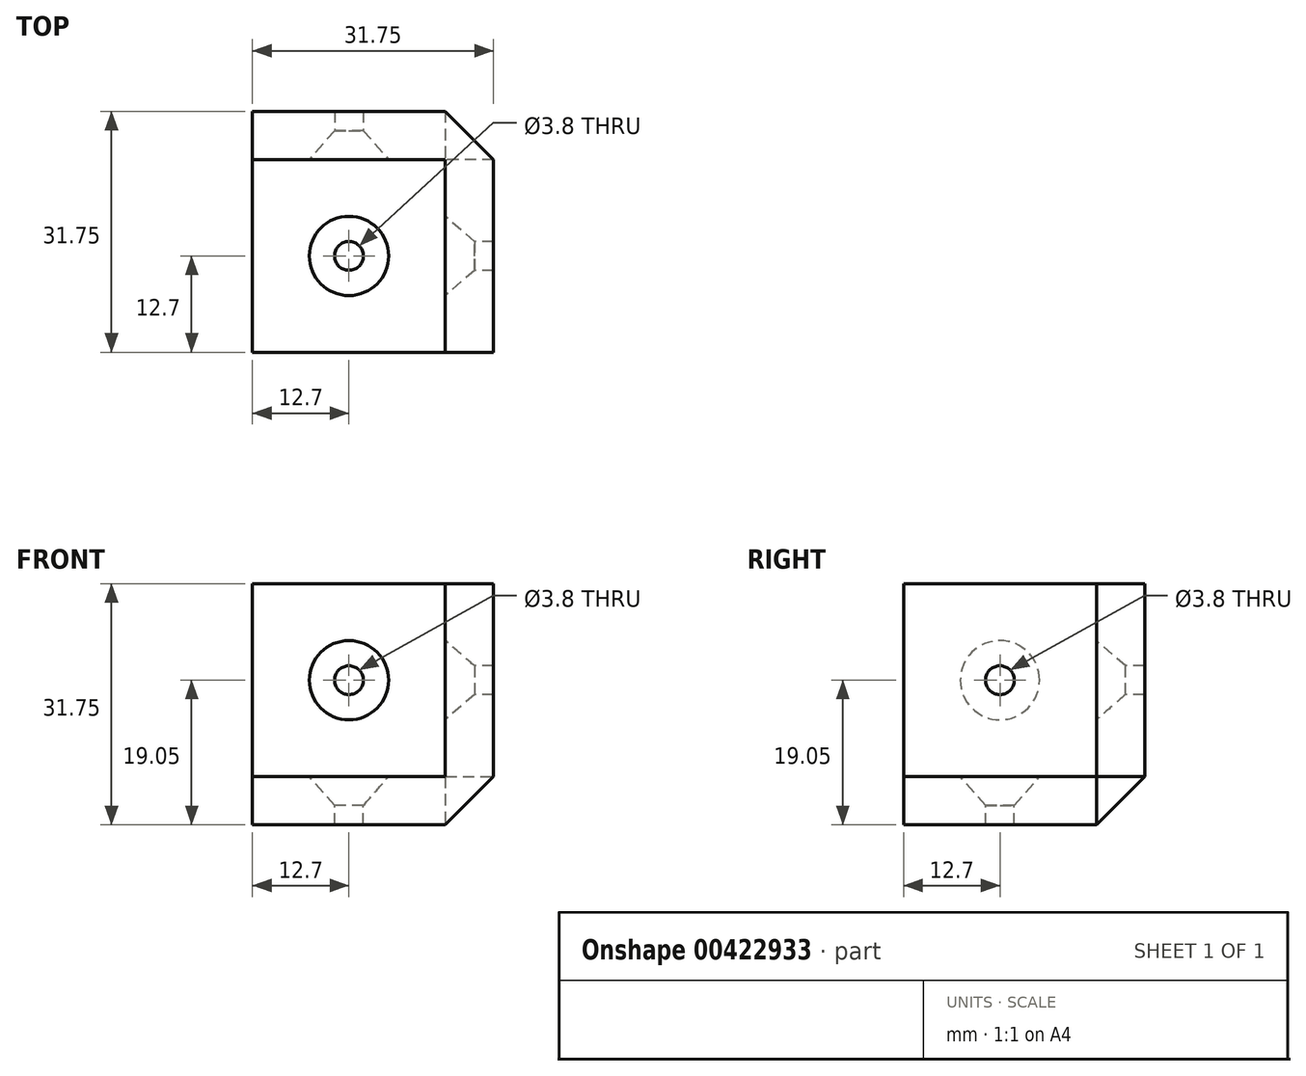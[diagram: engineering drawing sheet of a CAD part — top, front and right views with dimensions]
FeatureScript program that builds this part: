
annotation { "Feature Type Name" : "Feature", "Feature Type Description" : "" }
export const myFeature = defineFeature(function(context is Context, id is Id, definition is map)
    precondition{}
    {
        {
            var Q0;
            Q0=qCreatedBy(makeId("Top.planeOp"),FACE);
            var sketch = newSketch(context, id + "F0", { "sketchPlane" : qUnion([Q0])});
            skLineSegment(sketch, "E0.bottom", {"start": v(12.7, 12.7) * mm, "end": v(-12.7, 12.7) * mm});
            skLineSegment(sketch, "E0.top", {"start": v(12.7, -12.7) * mm, "end": v(-12.7, -12.7) * mm});
            skLineSegment(sketch, "E0.left", {"start": v(12.7, 12.7) * mm, "end": v(12.7, -12.7) * mm});
            skLineSegment(sketch, "E0.right", {"start": v(-12.7, 12.7) * mm, "end": v(-12.7, -12.7) * mm});
            skPoint(sketch, "E0.middle", {"position": v(0, 0) * mm});
            skSolve(sketch);
        }
        {
            var Q0;
            Q0 = qSketchRegion(id + "F0", true);
            extrude(context, id + "F1", {"entities" : qUnion([Q0]), "depth" : 6.35 * mm});
        }
        {
            var Q0;
            Q0=makeQuery(id+"F1.opExtrude","SWEPT_FACE",FACE,{"disambiguationData":[OSD([sQuery(id+"F0.wireOp",EDGE,"E0.left")])]});
            var sketch = newSketch(context, id + "F2", { "sketchPlane" : qUnion([Q0])});
            skLineSegment(sketch, "E1.bottom", {"start": v(-12.7, 0) * mm, "end": v(19.05, 0) * mm});
            skLineSegment(sketch, "E1.top", {"start": v(-12.7, 31.75) * mm, "end": v(19.05, 31.75) * mm});
            skLineSegment(sketch, "E1.left", {"start": v(-12.7, 0) * mm, "end": v(-12.7, 31.75) * mm});
            skLineSegment(sketch, "E1.right", {"start": v(19.05, 0) * mm, "end": v(19.05, 31.75) * mm});
            skSolve(sketch);
        }
        {
            var Q0;
            {var subQ4=sQuery(id+"F2.wireOp",EDGE,"E1.top");Q0=makeQuery(id+"F2.imprint","IMPRINT",FACE,{"disambiguationData":[TD([[makeQuery(id+"F2.imprint","IMPRINT",EDGE,{"derivedFrom":subQ4}),-1.0]])]});}
            var Q1;
            {var subQ1=sQuery(id+"F0.wireOp",EDGE,"E0.left");var subQ5=makeQuery(id+"F1.opExtrude","CAP_EDGE",EDGE,{"disambiguationData":[OSD([subQ1])],"isStart":false});Q1=makeQuery(id+"F2.imprint","IMPRINT",FACE,{"disambiguationData":[TD([[makeQuery(id+"F2.imprint","IMPRINT",EDGE,{"derivedFrom":subQ5}),1.0]])]});}
            extrude(context, id + "F3", {"entities" : qUnion([Q0, Q1]), "operationType" : NewBodyOperationType.ADD, "depth" : 6.35 * mm});
        }
        {
            var Q0;
            Q0=makeQuery(id+"F1.opExtrude","SWEPT_FACE",FACE,{"disambiguationData":[OSD([sQuery(id+"F0.wireOp",EDGE,"E0.bottom")])]});
            var sketch = newSketch(context, id + "F4", { "sketchPlane" : qUnion([Q0])});
            skLineSegment(sketch, "E2.bottom", {"start": v(12.7, 0) * mm, "end": v(-19.05, 0) * mm});
            skLineSegment(sketch, "E2.top", {"start": v(12.7, 31.75) * mm, "end": v(-19.05, 31.75) * mm});
            skLineSegment(sketch, "E2.left", {"start": v(12.7, 0) * mm, "end": v(12.7, 31.75) * mm});
            skLineSegment(sketch, "E2.right", {"start": v(-19.05, 0) * mm, "end": v(-19.05, 31.75) * mm});
            skSolve(sketch);
        }
        {
            var Q0;
            {var subQ0=sQuery(id+"F4.wireOp",EDGE,"E2.top");Q0=makeQuery(id+"F4.imprint","IMPRINT",FACE,{"disambiguationData":[TD([[makeQuery(id+"F4.imprint","IMPRINT",EDGE,{"derivedFrom":subQ0}),1.0]])]});}
            var Q1;
            {var subQ0=sQuery(id+"F4.wireOp",EDGE,"E2.bottom");Q1=makeQuery(id+"F4.imprint","IMPRINT",FACE,{"disambiguationData":[TD([[makeQuery(id+"F4.imprint","IMPRINT",EDGE,{"derivedFrom":subQ0}),1.0]])]});}
            extrude(context, id + "F5", {"entities" : qUnion([Q0, Q1]), "operationType" : NewBodyOperationType.ADD, "depth" : 6.35 * mm});
        }
        {
            var Q0;
            Q0=makeQuery(id+"F1.opExtrude","CAP_FACE",FACE,{"disambiguationData":[OSD([sQuery(id+"F0.wireOp",EDGE,"E0.bottom"),sQuery(id+"F0.wireOp",EDGE,"E0.top"),sQuery(id+"F0.wireOp",EDGE,"E0.left"),sQuery(id+"F0.wireOp",EDGE,"E0.right")])],"isStart":false});
            var sketch = newSketch(context, id + "F6", { "sketchPlane" : qUnion([Q0])});
            skCircle(sketch, "E3", {"center": v(0, 0) * mm, "radius": 3.18 * mm});
            skSolve(sketch);
        }
        {
            var Q0;
            Q0=makeQuery(id+"F5.opExtrude","CAP_FACE",FACE,{"disambiguationData":[OSD([sQuery(id+"F4.wireOp",EDGE,"E2.bottom"),sQuery(id+"F4.wireOp",EDGE,"E2.top"),sQuery(id+"F4.wireOp",EDGE,"E2.left"),sQuery(id+"F4.wireOp",EDGE,"E2.right")])],"isStart":true});
            var sketch = newSketch(context, id + "F7", { "sketchPlane" : qUnion([Q0])});
            skCircle(sketch, "E4", {"center": v(0, 19.05) * mm, "radius": 3.18 * mm});
            skSolve(sketch);
        }
        {
            var Q0;
            Q0=makeQuery(id+"F3.opExtrude","CAP_FACE",FACE,{"disambiguationData":[OSD([sQuery(id+"F2.wireOp",EDGE,"E1.bottom"),sQuery(id+"F2.wireOp",EDGE,"E1.top"),sQuery(id+"F2.wireOp",EDGE,"E1.left"),sQuery(id+"F2.wireOp",EDGE,"E1.right")])],"isStart":true});
            var sketch = newSketch(context, id + "F8", { "sketchPlane" : qUnion([Q0])});
            skCircle(sketch, "E5", {"center": v(0, 19.05) * mm, "radius": 3.18 * mm});
            skSolve(sketch);
        }
        {
            var Q0;
            Q0=sQuery(id+"F7.wireOp",VERTEX,"E4.center");
            var Q1;
            Q1=sQuery(id+"F6.wireOp",VERTEX,"E3.center");
            var Q2;
            Q2=sQuery(id+"F8.wireOp",VERTEX,"E5.center");
            var Q3;
            Q3=makeQuery(id+"F1.opExtrude","SWEPT_BODY",BODY,{"disambiguationData":[OSD([sQuery(id+"F0.wireOp",EDGE,"E0.bottom"),sQuery(id+"F0.wireOp",EDGE,"E0.top"),sQuery(id+"F0.wireOp",EDGE,"E0.left"),sQuery(id+"F0.wireOp",EDGE,"E0.right")])]});
            hole(context, id + "F9", {"style" : HoleStyle.C_SINK, "endStyle" : HoleEndStyle.THROUGH, "standardTappedOrClearance" : lookupTablePath({ "standard" : "ANSI", "engagement" : "75%", "pitch" : "24 tpi", "size" : "#10", "type" : "Tapped" }), "standardBlindInLast" : lookupTablePath({ "standard" : "ANSI", "engagement" : "75%", "pitch" : "24 tpi", "size" : "#10", "type" : "Tapped" }), "holeDiameter" : 3.8 * mm, "cSinkDiameter" : 10.44 * mm, "cSinkAngle" : 82 * degree, "showTappedDepth" : true, "isTappedThrough" : true, "tappedDepth" : 12.7 * mm, "tapClearance" : 3, "locations" : qUnion([Q0, Q1, Q2]), "scope" : qUnion([Q3]), "majorDiameter" : 4.83 * mm});
        }
        {
            var Q0;
            Q0=makeQuery(id+"F3.opExtrude","CAP_EDGE",EDGE,{"disambiguationData":[OSD([sQuery(id+"F2.wireOp",EDGE,"E1.right")])],"isStart":false});
            var Q1;
            Q1=makeQuery(id+"F3.opExtrude","CAP_EDGE",EDGE,{"disambiguationData":[OSD([sQuery(id+"F2.wireOp",EDGE,"E1.bottom")])],"isStart":false});
            var Q2;
            Q2=makeQuery(id+"F5.boolean.opBoolean","MERGE",EDGE,{"derivedFrom":[makeQuery(id+"F3.opExtrude","SWEPT_EDGE",EDGE,{"disambiguationData":[OSD([sQuery(id+"F2.wireOp",EDGE,"E1.bottom"),sQuery(id+"F2.wireOp",EDGE,"E1.right")])]}),makeQuery(id+"F5.opExtrude","CAP_EDGE",EDGE,{"disambiguationData":[OSD([sQuery(id+"F4.wireOp",EDGE,"E2.bottom")])],"isStart":false})]});
            chamfer(context, id + "F10", {"entities" : qUnion([Q0, Q1, Q2]), "width" : 6.35 * mm, "tangentPropagation" : true});
        }
    });
